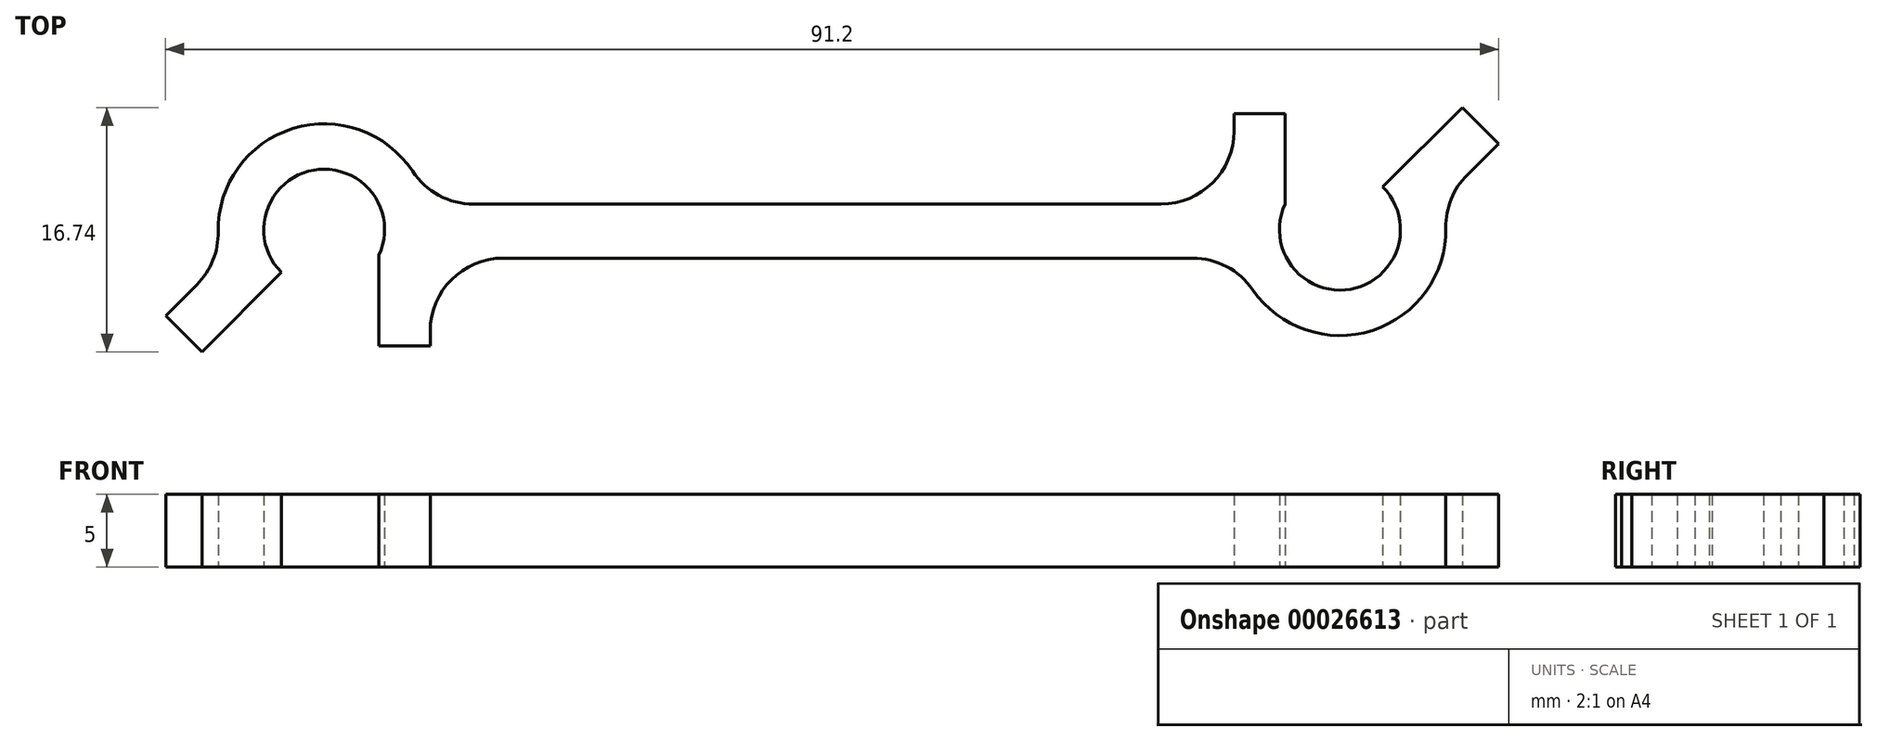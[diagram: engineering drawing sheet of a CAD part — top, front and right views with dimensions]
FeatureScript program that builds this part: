
annotation { "Feature Type Name" : "Feature", "Feature Type Description" : "" }
export const myFeature = defineFeature(function(context is Context, id is Id, definition is map)
    precondition{}
    {
        {
            var Q0;
            Q0=qCreatedBy(makeId("Top.planeOp"),FACE);
            var sketch = newSketch(context, id + "F0", { "sketchPlane" : qUnion([Q0])});
            skPoint(sketch, "E0.rect.middle", {"position": v(0, 0) * mm});
            skLineSegment(sketch, "E1", {"start": v(27.5, 6.75) * mm, "end": v(27.5, 7.95) * mm});
            skLineSegment(sketch, "E2", {"start": v(27.5, 7.95) * mm, "end": v(31, 7.95) * mm});
            skLineSegment(sketch, "E3", {"start": v(31, 7.95) * mm, "end": v(31, 1.75) * mm});
            skArc(sketch, "E4", {"start": v(28.78, -4.11) * mm, "mid": v(36.97, -6.9) * mm, "end": v(42, 0.13) * mm});
            skArc(sketch, "E5", {"start": v(31, 1.75) * mm, "mid": v(35.47, -4.08) * mm, "end": v(37.68, 2.93) * mm});
            skLineSegment(sketch, "E6", {"start": v(37.68, 2.93) * mm, "end": v(43.12, 8.37) * mm});
            skLineSegment(sketch, "E7", {"start": v(43.12, 8.37) * mm, "end": v(45.6, 5.9) * mm});
            skLineSegment(sketch, "E8", {"start": v(45.6, 5.9) * mm, "end": v(43.46, 3.76) * mm});
            skPoint(sketch, "E9.MirrorP", {"position": v(-27.5, -1.95) * mm});
            skLineSegment(sketch, "E10.MirrorCS", {"start": v(-43.12, -8.37) * mm, "end": v(-45.6, -5.9) * mm});
            skLineSegment(sketch, "E11.MirrorCS", {"start": v(-37.68, -2.93) * mm, "end": v(-43.12, -8.37) * mm});
            skArc(sketch, "E12.MirrorCS", {"start": v(-28.7, 4) * mm, "mid": v(-36.9, 6.92) * mm, "end": v(-42, -0.13) * mm});
            skArc(sketch, "E13.MirrorCS", {"start": v(-31, -1.75) * mm, "mid": v(-35.47, 4.08) * mm, "end": v(-37.68, -2.93) * mm});
            skLineSegment(sketch, "E14.MirrorCS", {"start": v(-45.6, -5.9) * mm, "end": v(-43.46, -3.76) * mm});
            skLineSegment(sketch, "E15.MirrorCS", {"start": v(-27.5, -7.95) * mm, "end": v(-31, -7.95) * mm});
            skLineSegment(sketch, "E16.MirrorCS", {"start": v(-27.5, -6.95) * mm, "end": v(-27.5, -7.95) * mm});
            skLineSegment(sketch, "E17.MirrorCS", {"start": v(-31, -7.95) * mm, "end": v(-31, -1.75) * mm});
            skLineSegment(sketch, "E18", {"start": v(-24.53, 1.75) * mm, "end": v(22.5, 1.75) * mm});
            skLineSegment(sketch, "E19", {"start": v(24.66, -1.95) * mm, "end": v(-22.5, -1.95) * mm});
            skPoint(sketch, "E20.visualSharp", {"position": v(-27.71, 1.75) * mm});
            skArc(sketch, "E20.filletArc", {"start": v(-28.7, 4) * mm, "mid": v(-26.9, 2.35) * mm, "end": v(-24.53, 1.75) * mm});
            skPoint(sketch, "E21.visualSharp", {"position": v(27.77, -1.95) * mm});
            skArc(sketch, "E21.filletArc", {"start": v(28.78, -4.11) * mm, "mid": v(26.99, -2.52) * mm, "end": v(24.66, -1.95) * mm});
            skArc(sketch, "E22.filletArc", {"start": v(-22.5, -1.95) * mm, "mid": v(-26.04, -3.41) * mm, "end": v(-27.5, -6.95) * mm});
            skPoint(sketch, "E23.visualSharp", {"position": v(27.5, 1.75) * mm});
            skArc(sketch, "E23.filletArc", {"start": v(22.5, 1.75) * mm, "mid": v(26.04, 3.21) * mm, "end": v(27.5, 6.75) * mm});
            skPoint(sketch, "E24.visualSharp", {"position": v(41.71, 2.01) * mm});
            skArc(sketch, "E24.filletArc", {"start": v(43.46, 3.76) * mm, "mid": v(42.36, 2.1) * mm, "end": v(42, 0.13) * mm});
            skPoint(sketch, "E25.visualSharp", {"position": v(-41.71, -2.01) * mm});
            skArc(sketch, "E25.filletArc", {"start": v(-43.46, -3.76) * mm, "mid": v(-42.36, -2.1) * mm, "end": v(-42, -0.13) * mm});
            skSolve(sketch);
        }
        {
            var Q0;
            Q0 = qSketchRegion(id + "F0", true);
            extrude(context, id + "F1", {"entities" : qUnion([Q0]), "depth" : 5 * mm});
        }
    });
